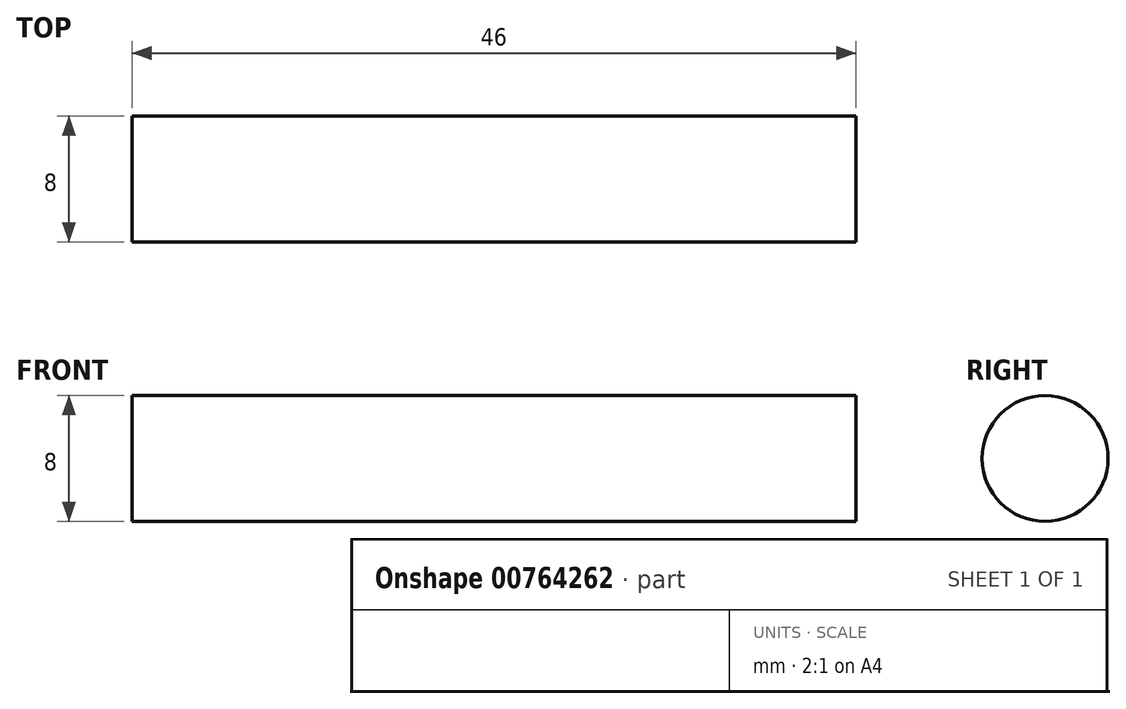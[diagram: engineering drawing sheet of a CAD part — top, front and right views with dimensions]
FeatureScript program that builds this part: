
annotation { "Feature Type Name" : "Feature", "Feature Type Description" : "" }
export const myFeature = defineFeature(function(context is Context, id is Id, definition is map)
    precondition{}
    {
        {
            var Q0;
            Q0=qCreatedBy(makeId("Right.planeOp"),FACE);
            var sketch = newSketch(context, id + "F0", { "sketchPlane" : qUnion([Q0])});
            skCircle(sketch, "E0", {"center": v(0, 0) * mm, "radius": 4 * mm});
            skSolve(sketch);
        }
        {
            var Q0;
            Q0 = qSketchRegion(id + "F0", true);
            extrude(context, id + "F1", {"entities" : qUnion([Q0]), "depth" : 46 * mm, "offsetDistance" : 25 * mm});
        }
    });
